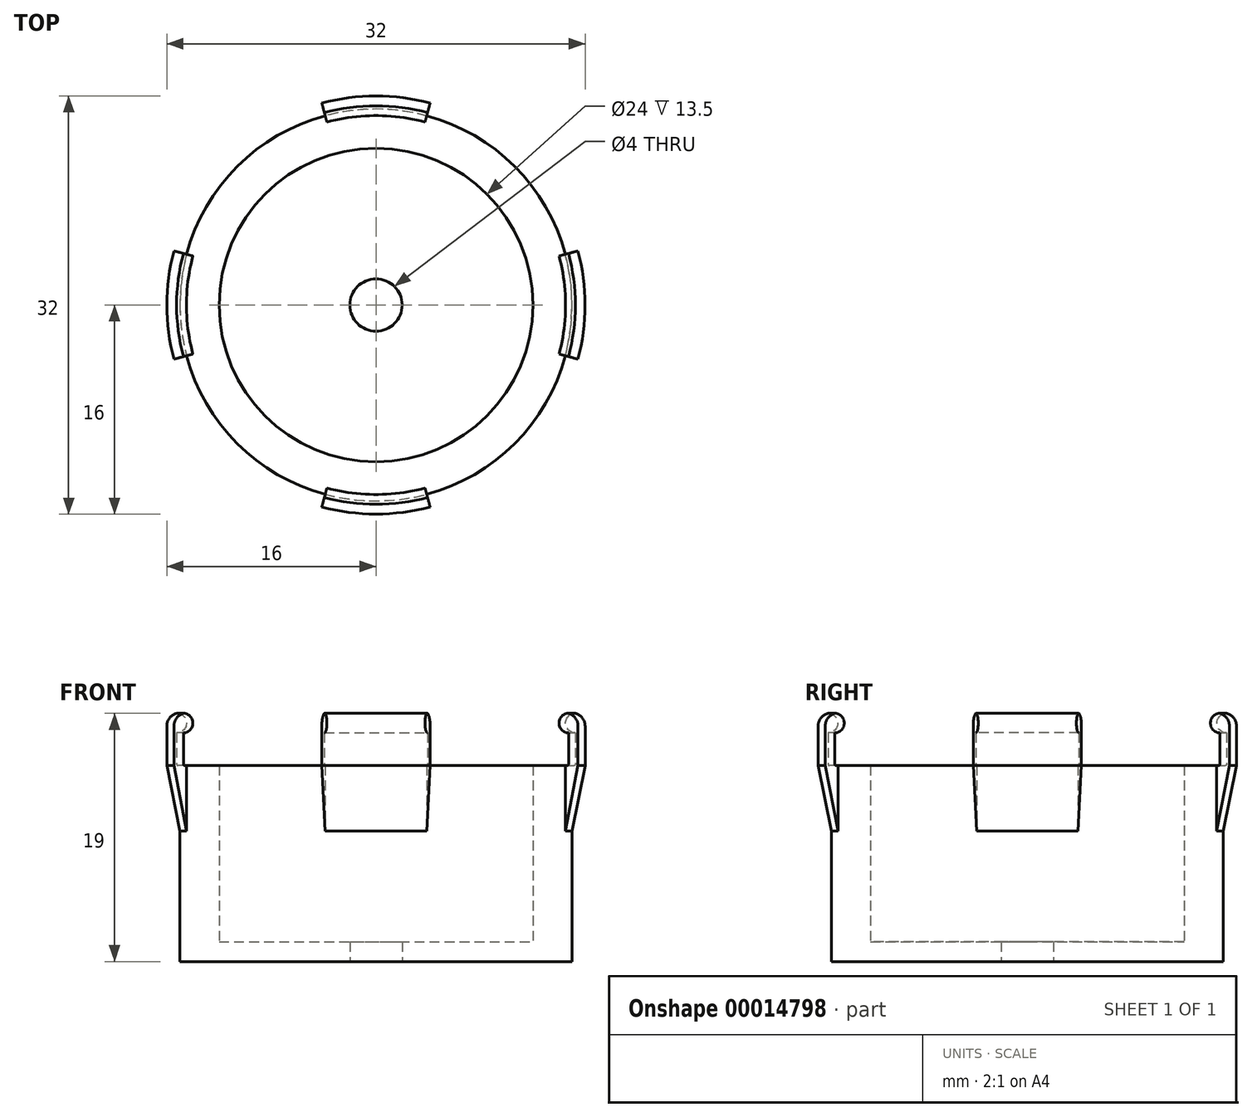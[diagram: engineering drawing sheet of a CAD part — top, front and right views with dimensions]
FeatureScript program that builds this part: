
annotation { "Feature Type Name" : "Feature", "Feature Type Description" : "" }
export const myFeature = defineFeature(function(context is Context, id is Id, definition is map)
    precondition{}
    {
        {
            var Q0;
            Q0=qCreatedBy(makeId("Front.planeOp"),FACE);
            var sketch = newSketch(context, id + "F0", { "sketchPlane" : qUnion([Q0])});
            skLineSegment(sketch, "E0.top", {"start": v(2, 1.5) * mm, "end": v(12, 1.5) * mm});
            skLineSegment(sketch, "E0.left", {"start": v(2, 0) * mm, "end": v(2, 1.5) * mm});
            skLineSegment(sketch, "E1.top", {"start": v(15, 15) * mm, "end": v(12, 15) * mm});
            skLineSegment(sketch, "E1.left", {"start": v(15, 0) * mm, "end": v(15, 15) * mm});
            skLineSegment(sketch, "E1.right", {"start": v(12, 1.5) * mm, "end": v(12, 15) * mm});
            skLineSegment(sketch, "E2", {"start": v(2, 0) * mm, "end": v(15, 0) * mm});
            skLineSegment(sketch, "E3", {"start": v(0, 0) * mm, "end": v(0, 17.07) * mm, "construction": true});
            skSolve(sketch);
        }
        {
            var Q0;
            Q0 = qSketchRegion(id + "F0", true);
            var Q1;
            Q1=sQuery(id+"F0.wireOp",EDGE,"E3");
            revolve(context, id + "F1", {"entities" : qUnion([Q0]), "axis" : qUnion([Q1]), "revolveType" : RevolveType.FULL});
        }
        {
            var Q0;
            Q0=qCreatedBy(makeId("Front.planeOp"),FACE);
            var sketch = newSketch(context, id + "F2", { "sketchPlane" : qUnion([Q0])});
            skLineSegment(sketch, "E4.bottom", {"start": v(15.25, 19) * mm, "end": v(16, 19) * mm});
            skLineSegment(sketch, "E4.left", {"start": v(15.25, 19) * mm, "end": v(15.25, 19) * mm});
            skLineSegment(sketch, "E5.top", {"start": v(15.15, 15) * mm, "end": v(14, 15) * mm});
            skLineSegment(sketch, "E5.right", {"start": v(14, 10) * mm, "end": v(14, 15) * mm});
            skLineSegment(sketch, "E6", {"start": v(14, 10) * mm, "end": v(15, 10) * mm});
            skLineSegment(sketch, "E7", {"start": v(16, 15) * mm, "end": v(16, 19) * mm});
            skLineSegment(sketch, "E8", {"start": v(15, 10) * mm, "end": v(16, 15) * mm});
            skArc(sketch, "E9", {"start": v(15.25, 19) * mm, "mid": v(14.5, 18.25) * mm, "end": v(15.25, 17.5) * mm});
            skLineSegment(sketch, "E10.trimOffspring", {"start": v(15.25, 17.5) * mm, "end": v(15.25, 15.1) * mm});
            skPoint(sketch, "E11.visualSharp", {"position": v(15.25, 15) * mm});
            skArc(sketch, "E11.filletArc", {"start": v(15.15, 15) * mm, "mid": v(15.22, 15.03) * mm, "end": v(15.25, 15.1) * mm});
            skSolve(sketch);
        }
        {
            var Q0;
            Q0 = qSketchRegion(id + "F2", true);
            var Q1;
            Q1=sQuery(id+"F0.wireOp",EDGE,"E3");
            revolve(context, id + "F3", {"entities" : qUnion([Q0]), "axis" : qUnion([Q1]), "revolveType" : RevolveType.SYMMETRIC, "angle" : 30 * degree});
        }
        {
            var Q0;
            Q0=makeQuery(id+"F3.opRevolve","SWEPT_BODY",BODY,{"disambiguationData":[OSD([sQuery(id+"F2.wireOp",EDGE,"E4.bottom"),sQuery(id+"F2.wireOp",EDGE,"E4.top"),sQuery(id+"F2.wireOp",EDGE,"E4.left"),sQuery(id+"F2.wireOp",EDGE,"E4.right")])]});
            var Q1;
            Q1=sQuery(id+"F0.wireOp",EDGE,"E3");
            circularPattern(context, id + "F4", {"operationType" : NewBodyOperationType.ADD, "entities" : qUnion([Q0]), "axis" : qUnion([Q1]), "angle" : 360 * degree, "instanceCount" : 4, "equalSpace" : true});
        }
        {
            var Q0;
            Q0=makeQuery(id+"F3.opRevolve","SWEPT_EDGE",EDGE,{"disambiguationData":[OSD([sQuery(id+"F2.wireOp",EDGE,"E4.bottom"),sQuery(id+"F2.wireOp",EDGE,"E7")])]});
            var Q1;
            Q1=makeQuery(id+"F4.opPattern","COPY",EDGE,{"derivedFrom":makeQuery(id+"F3.opRevolve","SWEPT_EDGE",EDGE,{"disambiguationData":[OSD([sQuery(id+"F2.wireOp",EDGE,"E4.bottom"),sQuery(id+"F2.wireOp",EDGE,"E7")])]}),"instanceName":"1"});
            var Q2;
            Q2=makeQuery(id+"F4.opPattern","COPY",EDGE,{"derivedFrom":makeQuery(id+"F3.opRevolve","SWEPT_EDGE",EDGE,{"disambiguationData":[OSD([sQuery(id+"F2.wireOp",EDGE,"E4.bottom"),sQuery(id+"F2.wireOp",EDGE,"E7")])]}),"instanceName":"2"});
            var Q3;
            Q3=makeQuery(id+"F4.opPattern","COPY",EDGE,{"derivedFrom":makeQuery(id+"F3.opRevolve","SWEPT_EDGE",EDGE,{"disambiguationData":[OSD([sQuery(id+"F2.wireOp",EDGE,"E4.bottom"),sQuery(id+"F2.wireOp",EDGE,"E7")])]}),"instanceName":"3"});
            fillet(context, id + "F5", {"entities" : qUnion([Q0, Q1, Q2, Q3]), "radius" : 1 * mm, "tangentPropagation" : true, "allowEdgeOverflow" : false});
        }
    });
